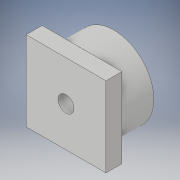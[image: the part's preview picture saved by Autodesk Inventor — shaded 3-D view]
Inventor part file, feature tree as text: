
AUTODESK INVENTOR PART (.ipt)
format: ipt  version: 2018 (Build 220112000, 112)  size: 109,568 bytes
history: native  units: mm
features: extrude x3, sketch x3
ambient origin geometry x8: Origin, YZ Plane, XZ Plane, XY Plane, X Axis, Y Axis, Z Axis, Center Point
bodies: Volumenkörper1 (feature_tree)
feature tree (6):
  extrude  "Extrusion1"  Depth=20.0mm TaperAngle=0.0deg
  extrude  "Extrusion2"  Depth=10.0mm
  extrude  "Extrusion3"  [1 undecoded]
  sketch  "Skizze1"  dims[d0=50.0mm d1=20.0mm d2=0.0mm]
  sketch  "Skizze2"  dims[d3=10.0mm d4=0.0mm d5=10.0mm]
  sketch  "Skizze3"  dims[d6=10.0mm d7=0.0mm]
note: 1 required parameter value undecoded (feature->parameter linkage not recoverable at this tier; creation-order binding heuristic only, values carry confidence <= 0.55)
